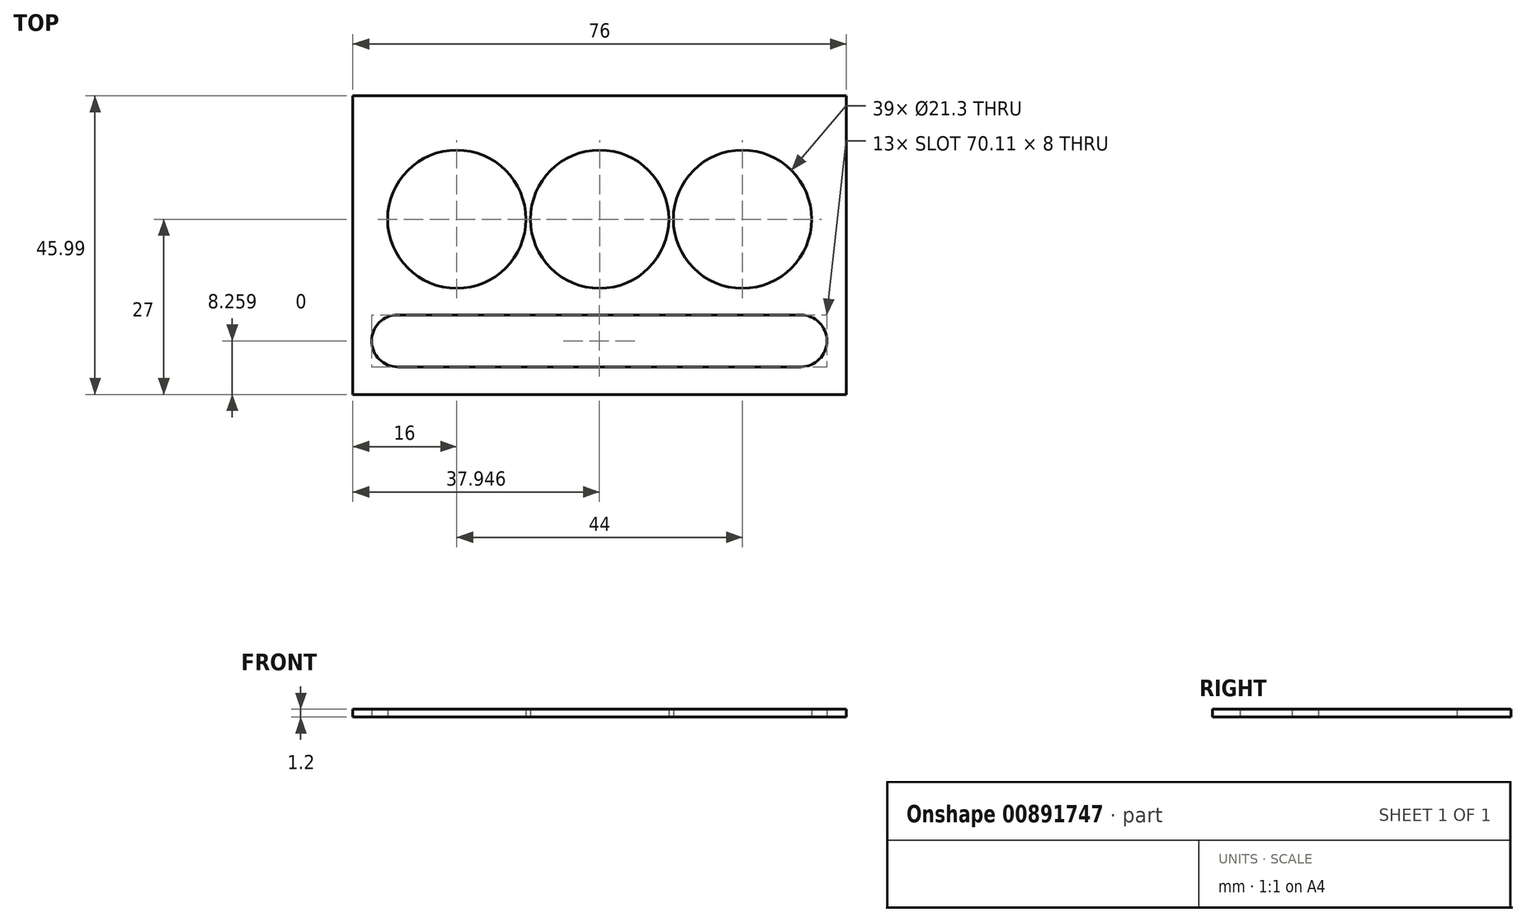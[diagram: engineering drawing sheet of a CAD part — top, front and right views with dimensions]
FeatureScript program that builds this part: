
annotation { "Feature Type Name" : "Feature", "Feature Type Description" : "" }
export const myFeature = defineFeature(function(context is Context, id is Id, definition is map)
    precondition{}
    {
        {
            var Q0;
            Q0=qCreatedBy(makeId("Top.planeOp"),FACE);
            var sketch = newSketch(context, id + "F0", { "sketchPlane" : qUnion([Q0])});
            skLineSegment(sketch, "E0.right", {"start": v(32, -23) * mm, "end": v(32, 23) * mm});
            skPoint(sketch, "E0.middle", {"position": v(0, 0) * mm});
            skPoint(sketch, "E1", {"position": v(16, 4) * mm});
            skCircle(sketch, "E2", {"center": v(16, 4) * mm, "radius": 10.65 * mm});
            skCircle(sketch, "E3", {"center": v(-6, 4) * mm, "radius": 10.65 * mm});
            skCircle(sketch, "E4", {"center": v(-28, 4) * mm, "radius": 10.65 * mm});
            skLineSegment(sketch, "E5", {"start": v(32, -23) * mm, "end": v(-44, -23) * mm});
            skLineSegment(sketch, "E6", {"start": v(25, -18.74) * mm, "end": v(-37.1, -18.74) * mm});
            skLineSegment(sketch, "E7", {"start": v(-44, -23) * mm, "end": v(-44, 23) * mm});
            skLineSegment(sketch, "E8", {"start": v(-37.1, -10.74) * mm, "end": v(25, -10.74) * mm});
            skArc(sketch, "E9", {"start": v(-37.1, -10.74) * mm, "mid": v(-41.1, -14.74) * mm, "end": v(-37.1, -18.74) * mm});
            skArc(sketch, "E10", {"start": v(25, -18.74) * mm, "mid": v(29, -14.74) * mm, "end": v(25, -10.74) * mm});
            skLineSegment(sketch, "E11", {"start": v(-44, 23) * mm, "end": v(32, 23) * mm});
            skSolve(sketch);
        }
        {
            var Q0;
            Q0 = qSketchRegion(id + "F0", true);
            extrude(context, id + "F1", {"entities" : qUnion([Q0]), "depth" : 1.2 * mm, "offsetDistance" : 25 * mm});
        }
    });
